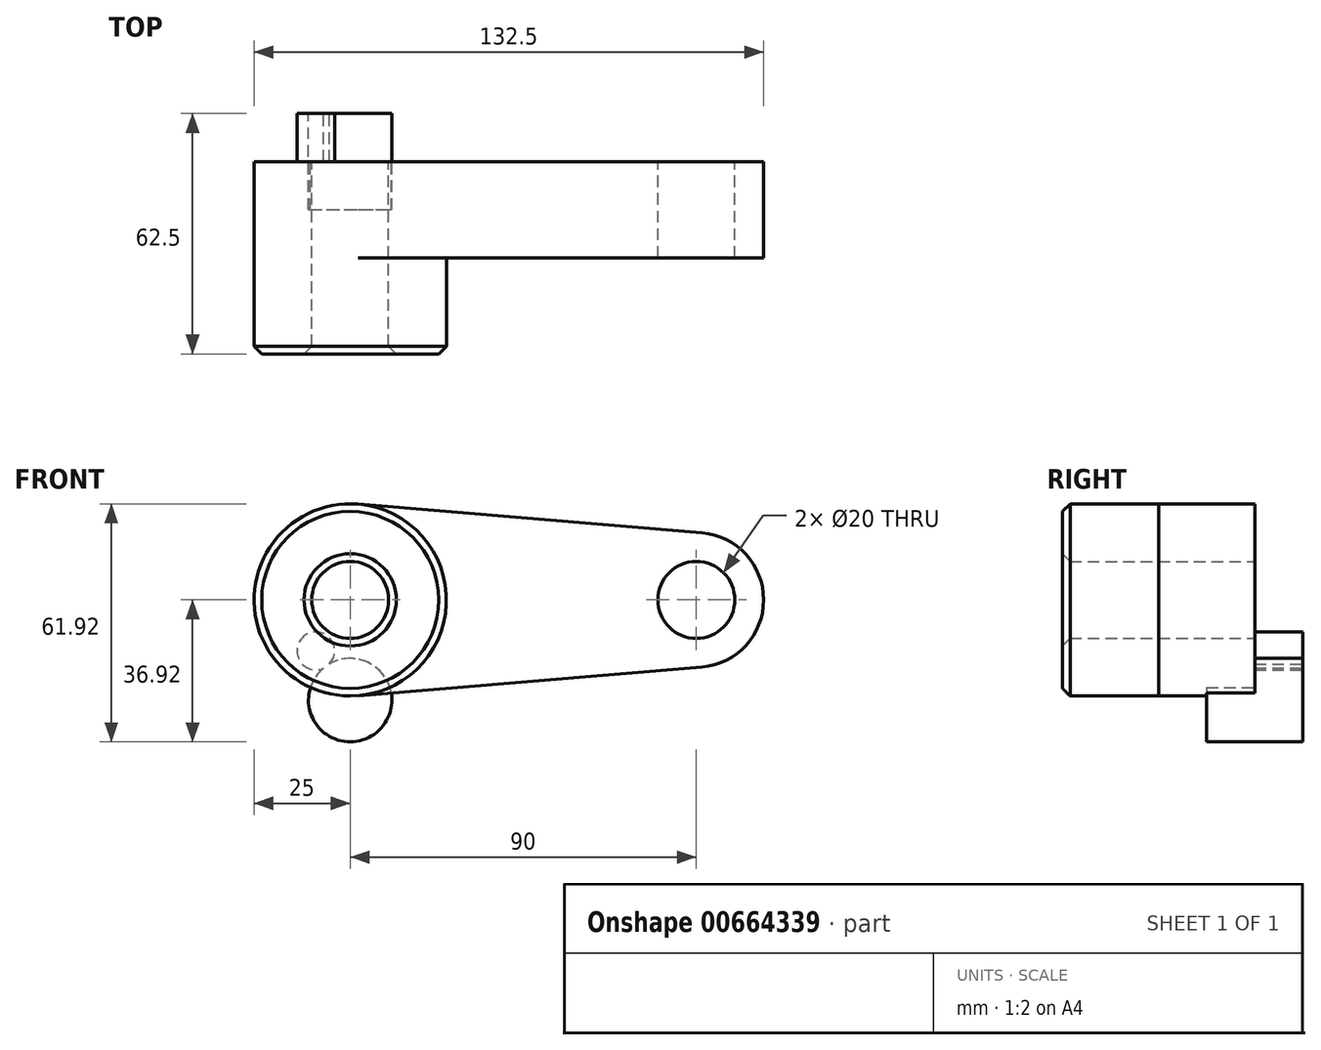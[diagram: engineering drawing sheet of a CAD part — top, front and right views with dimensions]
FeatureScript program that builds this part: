
annotation { "Feature Type Name" : "Feature", "Feature Type Description" : "" }
export const myFeature = defineFeature(function(context is Context, id is Id, definition is map)
    precondition{}
    {
        {
            var Q0;
            Q0=qCreatedBy(makeId("Front.planeOp"),FACE);
            var sketch = newSketch(context, id + "F0", { "sketchPlane" : qUnion([Q0])});
            skCircle(sketch, "E0", {"center": v(0, 0) * mm, "radius": 25 * mm});
            skCircle(sketch, "E1", {"center": v(90, 0) * mm, "radius": 17.5 * mm});
            skLineSegment(sketch, "E2", {"start": v(2.08, 24.91) * mm, "end": v(91.46, 17.44) * mm});
            skLineSegment(sketch, "E3", {"start": v(2.08, -24.91) * mm, "end": v(91.46, -17.44) * mm});
            skCircle(sketch, "E4", {"center": v(0, 0) * mm, "radius": 10 * mm});
            skCircle(sketch, "E5", {"center": v(90, 0) * mm, "radius": 10 * mm});
            skSolve(sketch);
        }
        {
            var Q0;
            Q0=qSketchRegion(id+"F0",true);
            extrude(context, id + "F1", {"entities" : qUnion([Q0]), "depth" : 25 * mm});
        }
        {
            var Q0;
            Q0=makeQuery(id+"F0.imprint","IMPRINT",FACE,{"disambiguationData":[TD([[makeQuery(id+"F0.imprint","IMPRINT",EDGE,{"derivedFrom":sQuery(id+"F0.wireOp",EDGE,"E4")}),-1.0]])]});
            extrude(context, id + "F2", {"entities" : qUnion([Q0]), "operationType" : NewBodyOperationType.ADD, "depth" : 50 * mm});
        }
        {
            var Q0;
            Q0=makeQuery(id+"F2.opExtrude","CAP_EDGE",EDGE,{"disambiguationData":[OSD([sQuery(id+"F0.wireOp",EDGE,"E0")])],"isStart":false});
            var Q1;
            Q1=makeQuery(id+"F2.opExtrude","CAP_EDGE",EDGE,{"disambiguationData":[OSD([sQuery(id+"F0.wireOp",EDGE,"E4")])],"isStart":false});
            var Q2;
            Q2=makeQuery(id+"F1.opExtrude","CAP_EDGE",EDGE,{"disambiguationData":[OSD([sQuery(id+"F0.wireOp",EDGE,"E5")])],"isStart":false});
            chamfer(context, id + "F3", {"entities" : qUnion([Q0, Q1, Q2]), "width" : 2 * mm, "tangentPropagation" : true});
        }
        {
            var Q0;
            Q0=makeQuery(id+"F0.imprint","IMPRINT",FACE,{"disambiguationData":[TD([[makeQuery(id+"F0.imprint","IMPRINT",EDGE,{"derivedFrom":sQuery(id+"F0.wireOp",EDGE,"E4")}),-1.0]])]});
            var sketch = newSketch(context, id + "F4", { "sketchPlane" : qUnion([Q0])});
            skCircle(sketch, "E6", {"center": v(-8.95, -13.26) * mm, "radius": 4.9 * mm});
            skCircle(sketch, "E7", {"center": v(0, -26.07) * mm, "radius": 10.84 * mm});
            skSolve(sketch);
        }
        {
            var Q0;
            Q0 = qSketchRegion(id + "F4", true);
            extrude(context, id + "F5", {"entities" : qUnion([Q0]), "operationType" : NewBodyOperationType.ADD, "endBound" : BoundingType.SYMMETRIC, "depth" : 25 * mm, "offsetDistance" : 25 * mm});
        }
        {
            var Q0;
            Q0 = qSketchRegion(id + "F0", true);
            var Q1;
            Q1=makeQuery(id+"F5.opExtrude","CAP_FACE",FACE,{"disambiguationData":[OSD([sQuery(id+"F4.wireOp",EDGE,"E6"),sQuery(id+"F4.wireOp",EDGE,"E7")])],"isStart":true});
            extrude(context, id + "F6", {"entities" : qUnion([Q0, Q1]), "operationType" : NewBodyOperationType.ADD, "depth" : 25 * mm, "offsetDistance" : 25 * mm});
        }
    });
